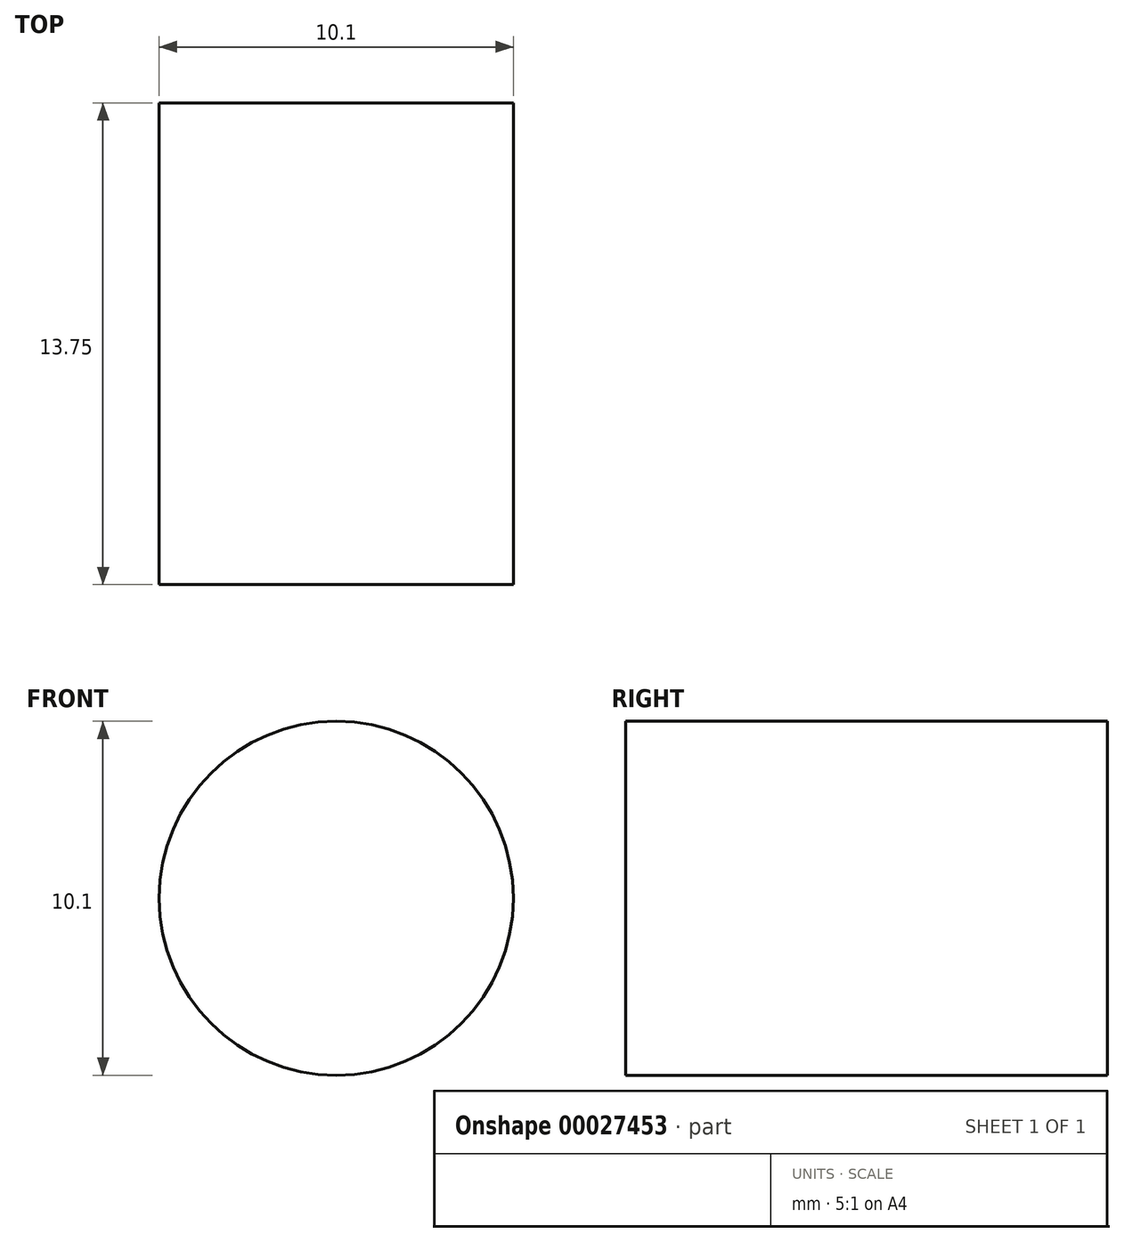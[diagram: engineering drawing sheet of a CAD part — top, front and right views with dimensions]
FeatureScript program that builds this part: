
annotation { "Feature Type Name" : "Feature", "Feature Type Description" : "" }
export const myFeature = defineFeature(function(context is Context, id is Id, definition is map)
    precondition{}
    {
        {
            var Q0;
            Q0=qCreatedBy(makeId("Front.planeOp"),FACE);
            var sketch = newSketch(context, id + "F0", { "sketchPlane" : qUnion([Q0])});
            skCircle(sketch, "E0", {"center": v(0, 0) * mm, "radius": 5.05 * mm});
            skSolve(sketch);
        }
        {
            var Q0;
            Q0 = qSketchRegion(id + "F0", true);
            extrude(context, id + "F1", {"entities" : qUnion([Q0]), "depth" : 13.75 * mm});
        }
    });
